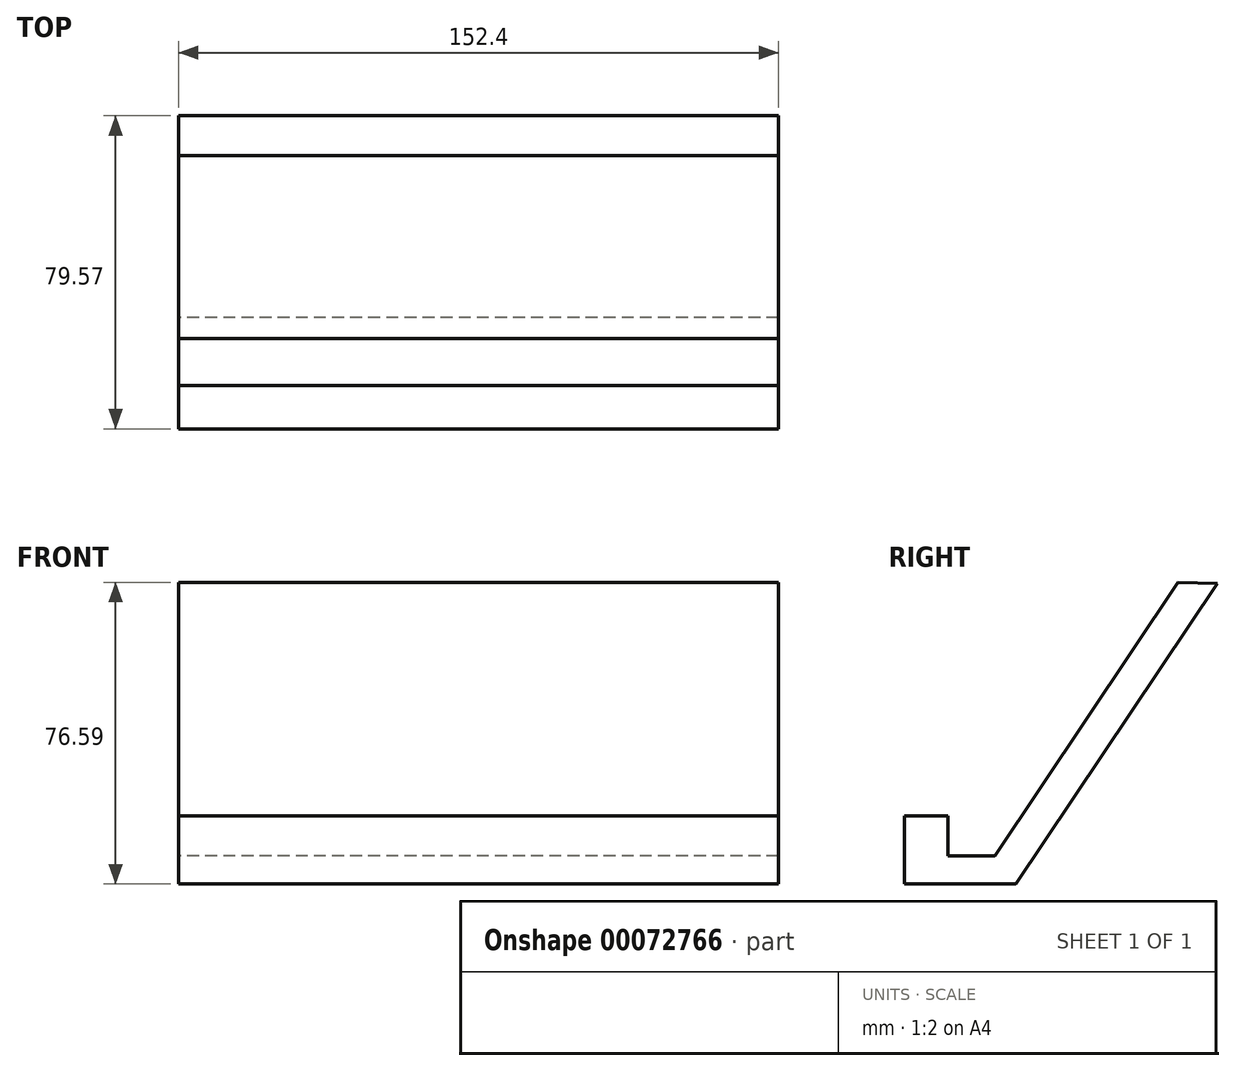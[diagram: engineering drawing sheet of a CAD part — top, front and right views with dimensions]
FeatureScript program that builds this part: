
annotation { "Feature Type Name" : "Feature", "Feature Type Description" : "" }
export const myFeature = defineFeature(function(context is Context, id is Id, definition is map)
    precondition{}
    {
        {
            var Q0;
            Q0=qCreatedBy(makeId("Right.planeOp"),FACE);
            var sketch = newSketch(context, id + "F0", { "sketchPlane" : qUnion([Q0])});
            skLineSegment(sketch, "E0", {"start": v(56.62, 31.44) * mm, "end": v(5.36, -44.85) * mm});
            skLineSegment(sketch, "E1", {"start": v(5.36, -44.85) * mm, "end": v(-22.95, -44.85) * mm});
            skLineSegment(sketch, "E2", {"start": v(-22.95, -44.85) * mm, "end": v(-22.95, -27.56) * mm});
            skLineSegment(sketch, "E3", {"start": v(-22.95, -27.56) * mm, "end": v(-11.92, -27.56) * mm});
            skLineSegment(sketch, "E4", {"start": v(-11.92, -27.56) * mm, "end": v(-11.92, -37.7) * mm});
            skLineSegment(sketch, "E5", {"start": v(-11.92, -37.7) * mm, "end": v(0, -37.7) * mm});
            skLineSegment(sketch, "E6", {"start": v(0, -37.7) * mm, "end": v(46.49, 31.74) * mm});
            skLineSegment(sketch, "E7", {"start": v(46.49, 31.74) * mm, "end": v(56.62, 31.44) * mm});
            skSolve(sketch);
        }
        {
            var Q0;
            Q0 = qSketchRegion(id + "F0", true);
            extrude(context, id + "F1", {"entities" : qUnion([Q0]), "depth" : 76.2 * mm, "hasSecondDirection" : true, "secondDirectionOppositeDirection" : true, "secondDirectionDepth" : 76.2 * mm});
        }
    });
